# Revit family: Скамейка «Мой Двор»
name_source: partatom
category: Мебель
revit_build: Autodesk Revit 2017 (Build: 20160225_1515(x64)
units: mm (PartAtom-declared; Revit-internal decimal feet)

## family parameters
Всегда вертикально = Да
Заголовок OmniClass = General Furniture and Specialties
На основе рабочей плоскости = Нет
Номер OmniClass = 23.40.20.00
Общий = Нет
При загрузке вырезать с полостями = Нет
Точка расчета площади = Нет

## types (7) — shared parameters
ADSK_Код изделия = 8083
ADSK_Материал доски = <По категории>
ADSK_Материал опоры = <По категории>
ADSK_Материал фурнитуры = <По категории>
ADSK_Размер_Высота = 770 мм
ADSK_Размер_Ширина = 757 мм
URL = https://hobbyka.ru
Изготовитель = ООО "Хоббика"

## per-type parameters (varying)
| type | ADSK_Размер_Длина | Длина доски | Перемычка | С_Количество_опор_Видимость | Стоимость |
| Скамейка «Мой Двор» 1,2м | 1200 мм | 1140 мм | Да | Нет | 7663 $ |
| Скамейка «Мой Двор» 1,5м | 1500 мм | 1440 мм | Да | Нет | 8214 $ |
| Скамейка «Мой Двор» 1,8м | 1800 мм | 1740 мм | Да | Нет | 9261 $ |
| Скамейка «Мой Двор» 2,0м (2 опоры) | 1800 мм | 1740 мм | Да | Нет | 9812 $ |
| Скамейка «Мой Двор» 2,0м | 1800 мм | 1740 мм | Нет | Да | 13892 $ |
| Скамейка «Мой Двор» 3,0м | 1800 мм | 1740 мм | Нет | Да | 14892 $ |
| Скамейка «Мой Двор» Кресло | 600 мм | 540 мм | Да | Нет | 7056 $ |

note: column(s) folded — value = type name in every type: ADSK_Наименование
